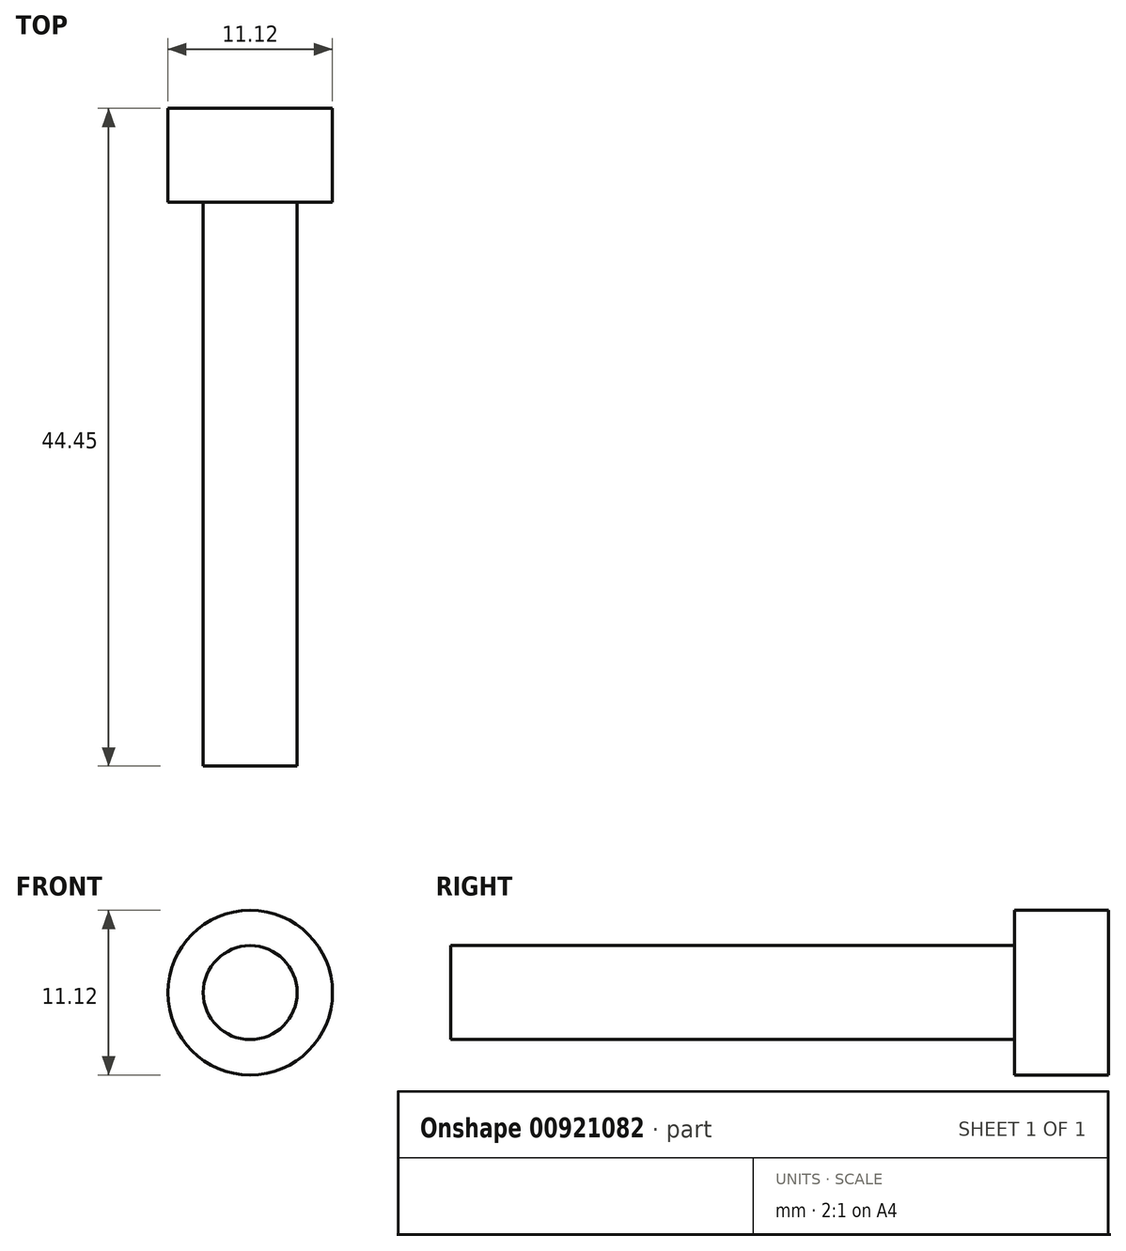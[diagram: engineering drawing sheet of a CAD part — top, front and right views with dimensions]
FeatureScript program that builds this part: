
annotation { "Feature Type Name" : "Feature", "Feature Type Description" : "" }
export const myFeature = defineFeature(function(context is Context, id is Id, definition is map)
    precondition{}
    {
        {
            var Q0;
            Q0=qCreatedBy(makeId("Front.planeOp"),FACE);
            var sketch = newSketch(context, id + "F0", { "sketchPlane" : qUnion([Q0])});
            skCircle(sketch, "E0", {"center": v(0, 0) * mm, "radius": 3.18 * mm});
            skSolve(sketch);
        }
        {
            var Q0;
            Q0 = qSketchRegion(id + "F0", true);
            extrude(context, id + "F1", {"entities" : qUnion([Q0]), "depth" : 38.1 * mm, "offsetDistance" : 25.4 * mm});
        }
        {
            var Q0;
            Q0=qCreatedBy(makeId("Front.planeOp"),FACE);
            var sketch = newSketch(context, id + "F2", { "sketchPlane" : qUnion([Q0])});
            skCircle(sketch, "E1", {"center": v(0, 0) * mm, "radius": 5.56 * mm});
            skSolve(sketch);
        }
        {
            var Q0;
            Q0 = qSketchRegion(id + "F2", true);
            extrude(context, id + "F3", {"entities" : qUnion([Q0]), "operationType" : NewBodyOperationType.ADD, "oppositeDirection" : true, "depth" : 6.35 * mm, "offsetDistance" : 25.4 * mm});
        }
    });
